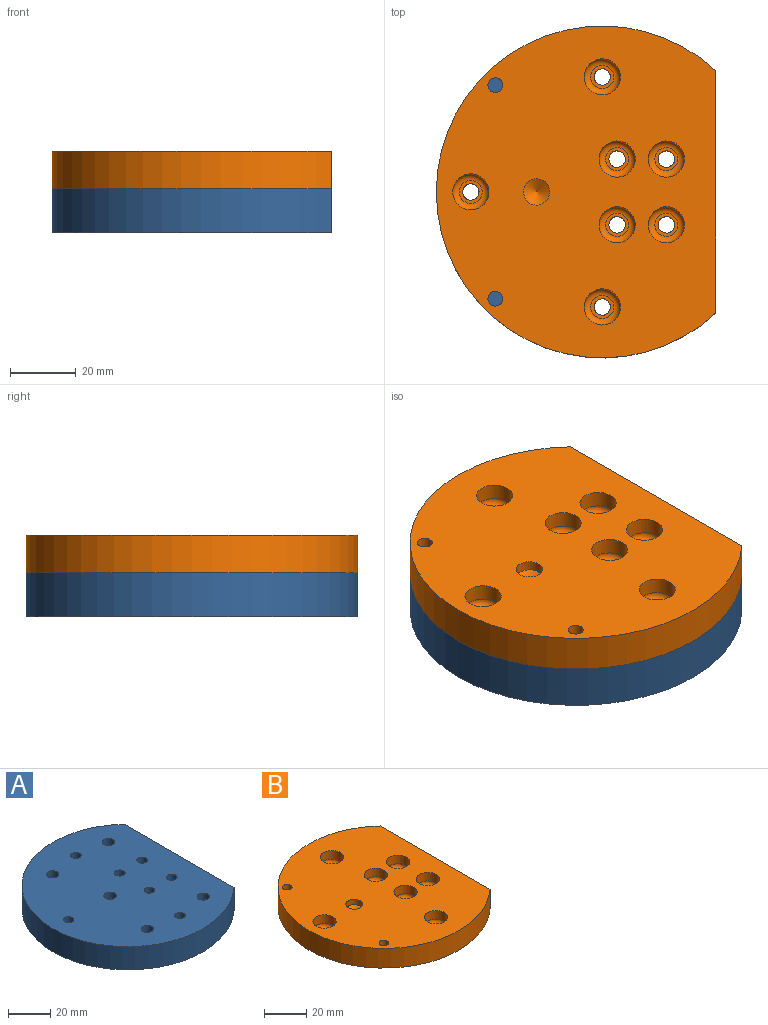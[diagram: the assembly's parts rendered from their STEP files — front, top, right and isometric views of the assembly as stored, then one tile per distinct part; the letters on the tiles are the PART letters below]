
ASSEMBLY  parts=2 mates=1
PART A: 30 faces, bbox 85x101x13.5 mm
  f0: plane 101x85mm, normal (0,0,-1), area 4439.5mm2, adj f2,f4,f5,f6,f9,f12,f15,f18
  f1: cylinder r=2.5mm len=5.2mm, axis (0,0,-1), area 81.7mm2, adj f7,f22
  f2: cylinder r=50.5mm len=101mm, axis (0,0,-1), area 3167.3mm2, adj f0,f3,f4
  f3: plane 101x85mm, normal (0,0,1), area 6922.6mm2, adj f2,f4,f8,f11,f14,f17,f21,f23
  f4: plane 73.76x13.5mm, normal (1,0,0), area 875.7mm2, adj f0,f2,f3,f5,f6,f7
  f5: plane 44.5x3mm, normal (0,1,0), area 133.5mm2, adj f0,f4,f7,f20
  f6: plane 44.5x3mm, normal (0,-1,0), area 133.5mm2, adj f0,f4,f7,f20
  f7: plane 64.5x40mm, normal (0,0,-1), area 2310.1mm2, adj f1,f4,f5,f6,f20,f23,f24,f27
  f8: cylinder r=2.93mm len=6.7mm, axis (0,0,-1), area 123.3mm2, adj f3,f10
  f9: cylinder r=4.8mm len=9.6mm, axis (0,0,-1), area 144.9mm2, adj f0,f10
  f10: torus R=2.8mm, axis (0,0,1), area 78.1mm2, adj f8,f9
  f11: cylinder r=2.93mm len=6.7mm, axis (0,0,-1), area 123.3mm2, adj f3,f13
  f12: cylinder r=4.8mm len=9.6mm, axis (0,0,-1), area 144.9mm2, adj f0,f13
  f13: torus R=2.8mm, axis (0,0,1), area 78.1mm2, adj f11,f12
  f14: cylinder r=2.93mm len=6.7mm, axis (0,0,-1), area 123.3mm2, adj f3,f16
  f15: cylinder r=4.8mm len=9.6mm, axis (0,0,-1), area 144.9mm2, adj f0,f16
  f16: torus R=2.8mm, axis (0,0,1), area 78.1mm2, adj f14,f15
  f17: cylinder r=2.93mm len=6.7mm, axis (0,0,-1), area 123.3mm2, adj f3,f19
  f18: cylinder r=4.8mm len=9.6mm, axis (0,0,-1), area 144.9mm2, adj f0,f19
  f19: torus R=2.8mm, axis (0,0,1), area 78.1mm2, adj f17,f18
  f20: cylinder r=20mm len=40mm, axis (0,0,1), area 188.5mm2, adj f0,f5,f6,f7
  f21: cylinder r=3mm len=6mm, axis (0,0,1), area 75mm2, adj f3,f22
  f22: torus R=1mm, axis (0,0,-1), area 25.7mm2, adj f1,f21
  f23: cylinder r=2.5mm len=10.5mm, axis (0,0,-1), area 164.9mm2, adj f3,f7
  f24: cylinder r=2.5mm len=10.5mm, axis (0,0,-1), area 164.9mm2, adj f3,f7
  f25: cylinder r=2.5mm len=13.5mm, axis (0,0,-1), area 212.1mm2, adj f0,f3
  f26: cylinder r=2.5mm len=13.5mm, axis (0,0,-1), area 212.1mm2, adj f0,f3
  f27: cylinder r=2.5mm len=10.5mm, axis (0,0,-1), area 164.9mm2, adj f3,f7
  f28: cylinder r=2.5mm len=10.5mm, axis (0,0,-1), area 164.9mm2, adj f3,f7
  f29: cylinder r=2.5mm len=13.5mm, axis (0,0,-1), area 212.1mm2, adj f0,f3
PART B: 42 faces, bbox 85x101x13.5 mm
  f0: plane 101x85mm, normal (0,0,-1), area 4697.2mm2, adj f1,f3,f4,f5,f7,f16,f19,f31
  f1: cylinder r=50.5mm len=101mm, axis (0,0,-1), area 2686.3mm2, adj f0,f2,f3
  f2: plane 101x85mm, normal (0,0,1), area 6448.9mm2, adj f1,f3,f12,f15,f18,f21,f27,f30
  f3: plane 73.76x13.5mm, normal (1,0,0), area 926.5mm2, adj f0,f1,f2,f4,f5,f6
  f4: plane 44.5x2.05mm, normal (0,-1,0), area 91.2mm2, adj f0,f3,f6,f7
  f5: plane 44.5x2.05mm, normal (0,1,0), area 91.2mm2, adj f0,f3,f6,f7
  f6: plane 64.5x40mm, normal (0,0,-1), area 2301.5mm2, adj f3,f4,f5,f7,f9,f10,f13,f25
  f7: cylinder r=20mm len=40mm, axis (0,0,1), area 128.8mm2, adj f0,f4,f5,f6
  f8: cone r=0mm half-angle=59deg, axis (0,0,-1), area 33mm2, adj f9
  f9: cylinder r=3mm len=7mm, axis (0,0,-1), area 131.9mm2, adj f6,f8
  f10: cylinder r=2.5mm len=6.5mm, axis (0,0,1), area 102.1mm2, adj f6,f11
  f11: plane 7x7mm, normal (0,0,1), area 18.8mm2, adj f10,f23
  f12: cylinder r=5.5mm len=11mm, axis (0,0,1), area 172.8mm2, adj f2,f23
  f13: cylinder r=2.5mm len=6.5mm, axis (0,0,1), area 102.1mm2, adj f6,f14
  f14: plane 7x7mm, normal (0,0,1), area 18.8mm2, adj f13,f24
  f15: cylinder r=5.5mm len=11mm, axis (0,0,1), area 172.8mm2, adj f2,f24
  f16: cylinder r=2.5mm len=5mm, axis (0,0,1), area 69.9mm2, adj f0,f17
  f17: plane 7x7mm, normal (0,0,1), area 18.8mm2, adj f16,f22
  f18: cylinder r=5.5mm len=11mm, axis (0,0,1), area 172.8mm2, adj f2,f22
  f19: cylinder r=2.5mm len=5mm, axis (0,0,1), area 69.9mm2, adj f0,f20
  f20: plane 7x7mm, normal (0,0,1), area 18.8mm2, adj f19,f37
  f21: cylinder r=5.5mm len=11mm, axis (0,0,1), area 172.8mm2, adj f2,f37
  f22: torus R=3.5mm, axis (0,0,1), area 94.2mm2, adj f17,f18
  f23: torus R=3.5mm, axis (0,0,1), area 94.2mm2, adj f11,f12
  f24: torus R=3.5mm, axis (0,0,1), area 94.2mm2, adj f14,f15
  f25: cylinder r=2.5mm len=6.5mm, axis (0,0,1), area 102.1mm2, adj f6,f26
  f26: plane 7x7mm, normal (0,0,1), area 18.8mm2, adj f25,f35
  f27: cylinder r=5.5mm len=11mm, axis (0,0,1), area 172.8mm2, adj f2,f35
  f28: cylinder r=2.5mm len=6.5mm, axis (0,0,1), area 102.1mm2, adj f6,f29
  f29: plane 7x7mm, normal (0,0,1), area 18.8mm2, adj f28,f36
  f30: cylinder r=5.5mm len=11mm, axis (0,0,1), area 172.8mm2, adj f2,f36
  f31: cylinder r=2.5mm len=5mm, axis (0,0,1), area 69.9mm2, adj f0,f32
  f32: plane 7x7mm, normal (0,0,1), area 18.8mm2, adj f31,f34
  f33: cylinder r=5.5mm len=11mm, axis (0,0,1), area 172.8mm2, adj f2,f34
  f34: torus R=3.5mm, axis (0,0,1), area 94.2mm2, adj f32,f33
  f35: torus R=3.5mm, axis (0,0,1), area 94.2mm2, adj f26,f27
  f36: torus R=3.5mm, axis (0,0,1), area 94.2mm2, adj f29,f30
  f37: torus R=3.5mm, axis (0,0,1), area 94.2mm2, adj f20,f21
  f38: cylinder r=2.25mm len=11.45mm, axis (0,0,1), area 161.9mm2, adj f0,f2
  f39: cylinder r=2.25mm len=11.45mm, axis (0,0,1), area 161.9mm2, adj f0,f2
  f40: cone r=0mm half-angle=59deg, axis (0,0,1), area 58.6mm2, adj f41
  f41: cylinder r=4mm len=8mm, axis (0,0,1), area 75.4mm2, adj f2,f40
PLACE A rot(axis=(1,0,0),180deg) t=(50.87,-31.78,12.7)mm
PLACE B t=(50.87,-31.78,12.7)mm
MATE fastened A.f25 <-> B.f19  axis (0,0,1) through (10.87,-31.78,12.7)mm
